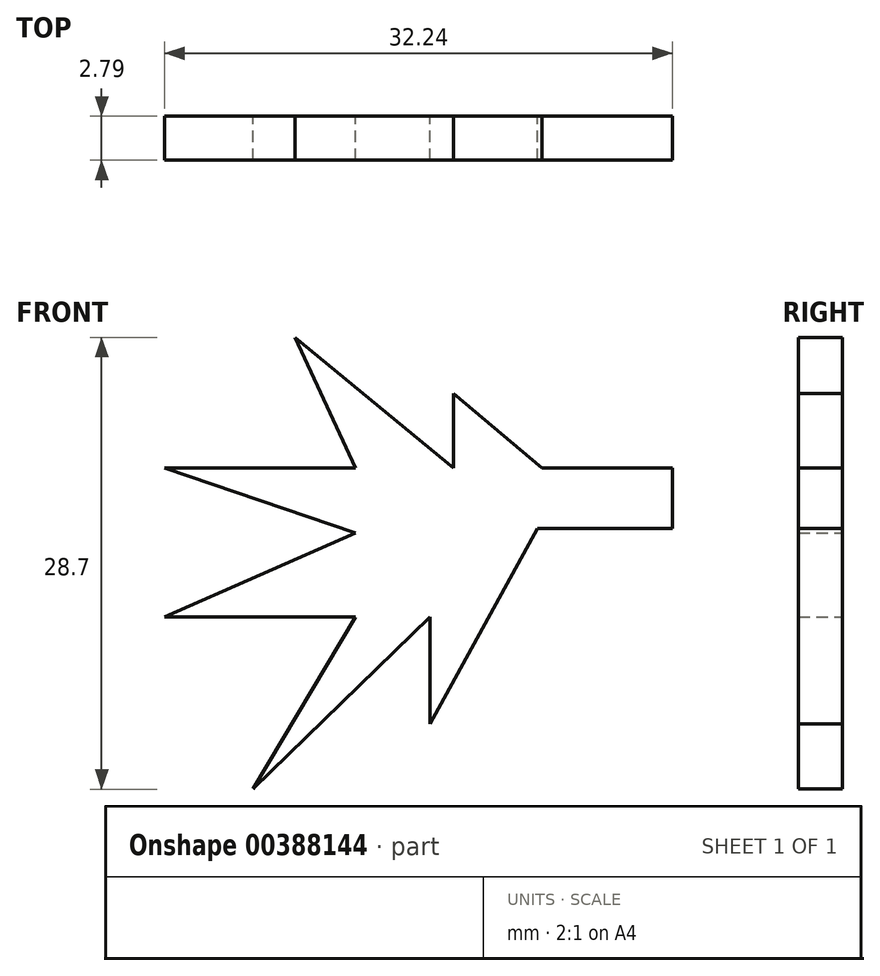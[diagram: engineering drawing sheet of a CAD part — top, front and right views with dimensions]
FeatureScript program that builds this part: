
annotation { "Feature Type Name" : "Feature", "Feature Type Description" : "" }
export const myFeature = defineFeature(function(context is Context, id is Id, definition is map)
    precondition{}
    {
        {
            var Q0;
            Q0=qCreatedBy(makeId("Front.planeOp"),FACE);
            var sketch = newSketch(context, id + "F0", { "sketchPlane" : qUnion([Q0])});
            skLineSegment(sketch, "E0", {"start": v(-132.52, -37.86) * mm, "end": v(-123.94, -37.86) * mm});
            skLineSegment(sketch, "E1", {"start": v(-123.94, -37.86) * mm, "end": v(-123.94, -34.02) * mm});
            skLineSegment(sketch, "E2", {"start": v(-123.94, -34.02) * mm, "end": v(-132.22, -34.02) * mm});
            skLineSegment(sketch, "E3", {"start": v(-132.22, -34.02) * mm, "end": v(-132.52, -37.86) * mm});
            skLineSegment(sketch, "E4", {"start": v(-132.22, -34.02) * mm, "end": v(-137.84, -29.28) * mm});
            skLineSegment(sketch, "E5", {"start": v(-137.84, -29.28) * mm, "end": v(-137.84, -34.02) * mm});
            skLineSegment(sketch, "E6", {"start": v(-137.84, -34.02) * mm, "end": v(-147.9, -25.73) * mm});
            skLineSegment(sketch, "E7", {"start": v(-147.9, -25.73) * mm, "end": v(-144.05, -34.02) * mm});
            skLineSegment(sketch, "E8", {"start": v(-144.05, -34.02) * mm, "end": v(-156.18, -34.02) * mm});
            skLineSegment(sketch, "E9", {"start": v(-156.18, -34.02) * mm, "end": v(-144.05, -38.16) * mm});
            skLineSegment(sketch, "E10", {"start": v(-144.05, -38.16) * mm, "end": v(-156.18, -43.48) * mm});
            skLineSegment(sketch, "E11", {"start": v(-156.18, -43.48) * mm, "end": v(-144.05, -43.48) * mm});
            skLineSegment(sketch, "E12", {"start": v(-144.05, -43.48) * mm, "end": v(-150.56, -54.43) * mm});
            skLineSegment(sketch, "E13", {"start": v(-150.56, -54.43) * mm, "end": v(-139.32, -43.48) * mm});
            skLineSegment(sketch, "E14", {"start": v(-139.32, -43.48) * mm, "end": v(-139.32, -50.29) * mm});
            skLineSegment(sketch, "E15", {"start": v(-139.32, -50.29) * mm, "end": v(-132.52, -37.86) * mm});
            skSolve(sketch);
        }
        {
            var Q0;
            Q0=makeQuery(id+"F0.imprint","IMPRINT",FACE,{"disambiguationData":[TD([[makeQuery(id+"F0.imprint","IMPRINT",EDGE,{"derivedFrom":sQuery(id+"F0.wireOp",EDGE,"E3")}),-1.0]])]});
            var Q1;
            Q1=makeQuery(id+"F0.imprint","IMPRINT",FACE,{"disambiguationData":[TD([[makeQuery(id+"F0.imprint","IMPRINT",EDGE,{"derivedFrom":sQuery(id+"F0.wireOp",EDGE,"E0")}),1.0]])]});
            extrude(context, id + "F1", {"entities" : qUnion([Q0, Q1]), "depth" : 2.8 * mm});
        }
    });
